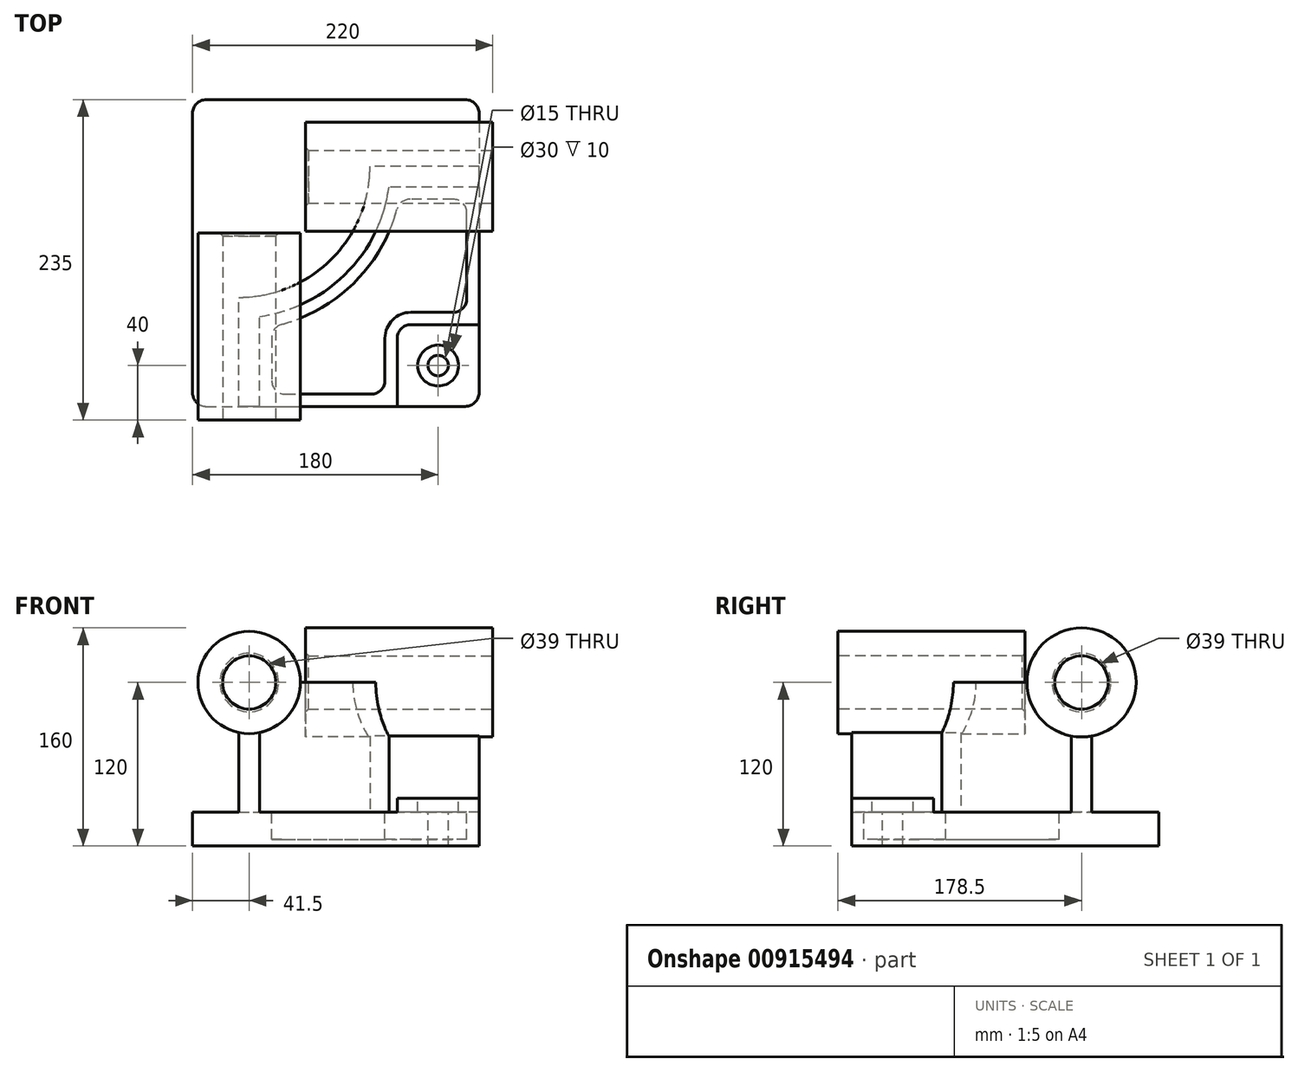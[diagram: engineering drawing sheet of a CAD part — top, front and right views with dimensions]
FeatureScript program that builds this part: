
annotation { "Feature Type Name" : "Feature", "Feature Type Description" : "" }
export const myFeature = defineFeature(function(context is Context, id is Id, definition is map)
    precondition{}
    {
        {
            var Q0;
            Q0=qCreatedBy(makeId("Top.planeOp"),FACE);
            var sketch = newSketch(context, id + "F0", { "sketchPlane" : qUnion([Q0])});
            skLineSegment(sketch, "E0.bottom", {"start": v(-105, 112.5) * mm, "end": v(105, 112.5) * mm});
            skLineSegment(sketch, "E0.top", {"start": v(-105, -112.5) * mm, "end": v(105, -112.5) * mm});
            skLineSegment(sketch, "E0.left", {"start": v(-105, 112.5) * mm, "end": v(-105, -112.5) * mm});
            skLineSegment(sketch, "E0.right", {"start": v(105, 112.5) * mm, "end": v(105, -112.5) * mm});
            skPoint(sketch, "E0.middle", {"position": v(0, 0) * mm});
            skSolve(sketch);
        }
        {
            var Q0;
            Q0=makeQuery(id+"F0.imprint","IMPRINT",FACE,{"disambiguationData":[TD([[makeQuery(id+"F0.imprint","IMPRINT",EDGE,{"derivedFrom":sQuery(id+"F0.wireOp",EDGE,"E0.bottom")}),-1.0]])]});
            extrude(context, id + "F1", {"entities" : qUnion([Q0]), "depth" : 25 * mm, "offsetDistance" : 25 * mm});
        }
        {
            var Q0;
            Q0=makeQuery(id+"F1.opExtrude","CAP_FACE",FACE,{"disambiguationData":[OSD([sQuery(id+"F0.wireOp",EDGE,"E0.bottom"),sQuery(id+"F0.wireOp",EDGE,"E0.top"),sQuery(id+"F0.wireOp",EDGE,"E0.left"),sQuery(id+"F0.wireOp",EDGE,"E0.right")])],"isStart":false});
            var sketch = newSketch(context, id + "F2", { "sketchPlane" : qUnion([Q0])});
            skLineSegment(sketch, "E1", {"start": v(-71, -112.5) * mm, "end": v(-71, -32.5) * mm});
            skLineSegment(sketch, "E2", {"start": v(105, 63.5) * mm, "end": v(25, 63.5) * mm});
            skArc(sketch, "E3", {"start": v(-71, -32.5) * mm, "mid": v(-3.12, -4.38) * mm, "end": v(25, 63.5) * mm});
            skLineSegment(sketch, "E4", {"start": v(-71, 63.5) * mm, "end": v(25, 63.5) * mm, "construction": true});
            skLineSegment(sketch, "E5", {"start": v(-71, 63.5) * mm, "end": v(-71, -32.5) * mm, "construction": true});
            skLineSegment(sketch, "E6.0", {"start": v(-56, -112.5) * mm, "end": v(-56, -46.48) * mm});
            skArc(sketch, "E6.1", {"start": v(-56, -46.48) * mm, "mid": v(7.49, -14.99) * mm, "end": v(38.98, 48.5) * mm});
            skLineSegment(sketch, "E6.2", {"start": v(105, 48.5) * mm, "end": v(38.98, 48.5) * mm});
            skLineSegment(sketch, "E7.0", {"start": v(105, 112.5) * mm, "end": v(105, -112.5) * mm});
            skLineSegment(sketch, "E8.0", {"start": v(-105, -112.5) * mm, "end": v(105, -112.5) * mm});
            skSolve(sketch);
        }
        {
            var Q0;
            {var subQ2=sQuery(id+"F2.wireOp",EDGE,"E1");Q0=makeQuery(id+"F2.imprint","IMPRINT",FACE,{"disambiguationData":[TD([[makeQuery(id+"F2.imprint","IMPRINT",EDGE,{"derivedFrom":subQ2}),-1.0]])]});}
            extrude(context, id + "F3", {"entities" : qUnion([Q0]), "operationType" : NewBodyOperationType.ADD, "depth" : 95 * mm, "offsetDistance" : 25 * mm});
        }
        {
            var Q0;
            Q0=makeQuery(id+"F3.boolean.opBoolean","MERGE",FACE,{"derivedFrom":[makeQuery(id+"F1.opExtrude","SWEPT_FACE",FACE,{"disambiguationData":[OSD([sQuery(id+"F0.wireOp",EDGE,"E0.top")])]}),makeQuery(id+"F3.opExtrude","SWEPT_FACE",FACE,{"disambiguationData":[OSD([sQuery(id+"F2.wireOp",EDGE,"E8.0")])]})]});
            var sketch = newSketch(context, id + "F4", { "sketchPlane" : qUnion([Q0])});
            skCircle(sketch, "E9", {"center": v(-63.5, 120) * mm, "radius": 37.5 * mm});
            skSolve(sketch);
        }
        {
            var Q0;
            Q0 = qSketchRegion(id + "F4", true);
            extrude(context, id + "F5", {"entities" : qUnion([Q0]), "operationType" : NewBodyOperationType.ADD, "depth" : 10 * mm, "offsetDistance" : 25 * mm, "hasSecondDirection" : true, "secondDirectionOppositeDirection" : true, "secondDirectionDepth" : 127.1 * mm});
        }
        {
            var Q0;
            Q0=makeQuery(id+"F3.boolean.opBoolean","MERGE",FACE,{"derivedFrom":[makeQuery(id+"F1.opExtrude","SWEPT_FACE",FACE,{"disambiguationData":[OSD([sQuery(id+"F0.wireOp",EDGE,"E0.right")])]}),makeQuery(id+"F3.opExtrude","SWEPT_FACE",FACE,{"disambiguationData":[OSD([sQuery(id+"F2.wireOp",EDGE,"E7.0")])]})]});
            var sketch = newSketch(context, id + "F6", { "sketchPlane" : qUnion([Q0])});
            skCircle(sketch, "E10", {"center": v(56, 120) * mm, "radius": 40 * mm});
            skSolve(sketch);
        }
        {
            var Q0;
            Q0 = qSketchRegion(id + "F6", true);
            extrude(context, id + "F7", {"entities" : qUnion([Q0]), "operationType" : NewBodyOperationType.ADD, "depth" : 10 * mm, "offsetDistance" : 25 * mm, "hasSecondDirection" : true, "secondDirectionOppositeDirection" : true, "secondDirectionDepth" : 127.1 * mm});
        }
        {
            var Q0;
            {var subQ0=sQuery(id+"F0.wireOp",EDGE,"E0.right");var subQ1=sQuery(id+"F0.wireOp",EDGE,"E0.top");Q0=makeQuery(id+"F3.boolean.opBoolean","SPLIT",FACE,{"disambiguationData":[TD([makeQuery(id+"F3.opExtrude","SWEPT_FACE",FACE,{"disambiguationData":[OSD([sQuery(id+"F2.wireOp",EDGE,"E6.0")])]})])],"derivedFrom":makeQuery(id+"F1.opExtrude","CAP_FACE",FACE,{"disambiguationData":[OSD([sQuery(id+"F0.wireOp",EDGE,"E0.bottom"),subQ1,sQuery(id+"F0.wireOp",EDGE,"E0.left"),subQ0])],"isStart":false})});}
            var sketch = newSketch(context, id + "F8", { "sketchPlane" : qUnion([Q0])});
            skLineSegment(sketch, "E11.bottom", {"start": v(105, -112.5) * mm, "end": v(45, -112.5) * mm});
            skLineSegment(sketch, "E11.top", {"start": v(105, -52.5) * mm, "end": v(45, -52.5) * mm});
            skLineSegment(sketch, "E11.left", {"start": v(105, -112.5) * mm, "end": v(105, -52.5) * mm});
            skLineSegment(sketch, "E11.right", {"start": v(45, -112.5) * mm, "end": v(45, -52.5) * mm});
            skSolve(sketch);
        }
        {
            var Q0;
            Q0 = qSketchRegion(id + "F8", true);
            extrude(context, id + "F9", {"entities" : qUnion([Q0]), "operationType" : NewBodyOperationType.ADD, "depth" : (35 - 25) * mm, "offsetDistance" : 25 * mm});
        }
        {
            var Q0;
            Q0=makeQuery(id+"F9.opExtrude","SWEPT_EDGE",EDGE,{"disambiguationData":[OSD([sQuery(id+"F8.wireOp",EDGE,"E11.top"),sQuery(id+"F8.wireOp",EDGE,"E11.right")])]});
            fillet(context, id + "F10", {"entities" : qUnion([Q0]), "radius" : 10 * mm, "tangentPropagation" : true, "allowEdgeOverflow" : false});
        }
        {
            var Q0;
            {var subQ0=sQuery(id+"F0.wireOp",EDGE,"E0.right");var subQ1=sQuery(id+"F0.wireOp",EDGE,"E0.top");Q0=makeQuery(id+"F3.boolean.opBoolean","SPLIT",FACE,{"disambiguationData":[TD([makeQuery(id+"F3.opExtrude","SWEPT_FACE",FACE,{"disambiguationData":[OSD([sQuery(id+"F2.wireOp",EDGE,"E6.0")])]})])],"derivedFrom":makeQuery(id+"F1.opExtrude","CAP_FACE",FACE,{"disambiguationData":[OSD([sQuery(id+"F0.wireOp",EDGE,"E0.bottom"),subQ1,sQuery(id+"F0.wireOp",EDGE,"E0.left"),subQ0])],"isStart":false})});}
            var sketch = newSketch(context, id + "F11", { "sketchPlane" : qUnion([Q0])});
            skLineSegment(sketch, "E12.0", {"start": v(-47, -54.08) * mm, "end": v(-47, -103.5) * mm});
            skArc(sketch, "E12.1", {"start": v(46.58, 39.5) * mm, "mid": v(13.85, -21.35) * mm, "end": v(-47, -54.08) * mm});
            skLineSegment(sketch, "E12.2", {"start": v(-47, -103.5) * mm, "end": v(36, -103.5) * mm});
            skLineSegment(sketch, "E12.3", {"start": v(96, 39.5) * mm, "end": v(46.58, 39.5) * mm});
            skLineSegment(sketch, "E12.4", {"start": v(36, -103.5) * mm, "end": v(36, -62.5) * mm});
            skArc(sketch, "E12.5", {"start": v(36, -62.5) * mm, "mid": v(41.56, -49.06) * mm, "end": v(55, -43.5) * mm});
            skLineSegment(sketch, "E12.6", {"start": v(55, -43.5) * mm, "end": v(96, -43.5) * mm});
            skLineSegment(sketch, "E12.7", {"start": v(96, -43.5) * mm, "end": v(96, 39.5) * mm});
            skSolve(sketch);
        }
        {
            var Q0;
            Q0=makeQuery(id+"F11.imprint","IMPRINT",FACE,{"disambiguationData":[TD([[makeQuery(id+"F11.imprint","IMPRINT",EDGE,{"derivedFrom":sQuery(id+"F11.wireOp",EDGE,"E12.0")}),1.0]])]});
            extrude(context, id + "F12", {"entities" : qUnion([Q0]), "operationType" : NewBodyOperationType.REMOVE, "oppositeDirection" : true, "depth" : (25 - 5) * mm, "offsetDistance" : 25 * mm});
        }
        {
            var Q0;
            Q0=makeQuery(id+"F9.opExtrude","CAP_FACE",FACE,{"disambiguationData":[OSD([sQuery(id+"F8.wireOp",EDGE,"E11.bottom"),sQuery(id+"F8.wireOp",EDGE,"E11.top"),sQuery(id+"F8.wireOp",EDGE,"E11.left"),sQuery(id+"F8.wireOp",EDGE,"E11.right")])],"isStart":false});
            var sketch = newSketch(context, id + "F13", { "sketchPlane" : qUnion([Q0])});
            skCircle(sketch, "E13", {"center": v(75, -82.5) * mm, "radius": 15 * mm});
            skSolve(sketch);
        }
        {
            var Q0;
            Q0=sQuery(id+"F13.wireOp",VERTEX,"E13.center");
            var Q1;
            Q1=makeQuery(id+"F1.opExtrude","SWEPT_BODY",BODY,{"disambiguationData":[OSD([sQuery(id+"F0.wireOp",EDGE,"E0.bottom"),sQuery(id+"F0.wireOp",EDGE,"E0.top"),sQuery(id+"F0.wireOp",EDGE,"E0.left"),sQuery(id+"F0.wireOp",EDGE,"E0.right")])]});
            hole(context, id + "F14", {"style" : HoleStyle.C_BORE, "endStyle" : HoleEndStyle.THROUGH, "holeDiameter" : 15 * mm, "cBoreDiameter" : 30 * mm, "cBoreDepth" : 10 * mm, "majorDiameter" : 5 * mm, "isTappedThrough" : true, "tappedDepth" : 12 * mm, "tapClearance" : 3, "locations" : qUnion([Q0]), "scope" : qUnion([Q1])});
        }
        {
            var Q0;
            Q0=makeQuery(id+"F12.boolean.opBoolean","COPY",EDGE,{"derivedFrom":makeQuery(id+"F12.opExtrude","SWEPT_EDGE",EDGE,{"disambiguationData":[OSD([sQuery(id+"F11.wireOp",EDGE,"E12.0"),sQuery(id+"F11.wireOp",EDGE,"E12.1")])]})});
            var Q1;
            Q1=makeQuery(id+"F12.boolean.opBoolean","COPY",EDGE,{"derivedFrom":makeQuery(id+"F12.opExtrude","SWEPT_EDGE",EDGE,{"disambiguationData":[OSD([sQuery(id+"F11.wireOp",EDGE,"E12.1"),sQuery(id+"F11.wireOp",EDGE,"E12.3")])]})});
            var Q2;
            Q2=makeQuery(id+"F12.boolean.opBoolean","COPY",EDGE,{"derivedFrom":makeQuery(id+"F12.opExtrude","SWEPT_EDGE",EDGE,{"disambiguationData":[OSD([sQuery(id+"F11.wireOp",EDGE,"E12.0"),sQuery(id+"F11.wireOp",EDGE,"E12.2")])]})});
            var Q3;
            Q3=makeQuery(id+"F12.boolean.opBoolean","COPY",EDGE,{"derivedFrom":makeQuery(id+"F12.opExtrude","SWEPT_EDGE",EDGE,{"disambiguationData":[OSD([sQuery(id+"F11.wireOp",EDGE,"E12.2"),sQuery(id+"F11.wireOp",EDGE,"E12.4")])]})});
            var Q4;
            Q4=makeQuery(id+"F12.boolean.opBoolean","COPY",EDGE,{"derivedFrom":makeQuery(id+"F12.opExtrude","SWEPT_EDGE",EDGE,{"disambiguationData":[OSD([sQuery(id+"F11.wireOp",EDGE,"E12.6"),sQuery(id+"F11.wireOp",EDGE,"E12.7")])]})});
            var Q5;
            Q5=makeQuery(id+"F12.boolean.opBoolean","COPY",EDGE,{"derivedFrom":makeQuery(id+"F12.opExtrude","SWEPT_EDGE",EDGE,{"disambiguationData":[OSD([sQuery(id+"F11.wireOp",EDGE,"E12.3"),sQuery(id+"F11.wireOp",EDGE,"E12.7")])]})});
            fillet(context, id + "F15", {"entities" : qUnion([Q0, Q1, Q2, Q3, Q4, Q5]), "radius" : 10 * mm, "tangentPropagation" : true, "allowEdgeOverflow" : false});
        }
        {
            var Q0;
            Q0=makeQuery(id+"F5.opExtrude","CAP_FACE",FACE,{"disambiguationData":[OSD([sQuery(id+"F4.wireOp",EDGE,"E9")])],"isStart":false});
            var sketch = newSketch(context, id + "F16", { "sketchPlane" : qUnion([Q0])});
            skCircle(sketch, "E14", {"center": v(-63.5, 120) * mm, "radius": 19.5 * mm});
            skSolve(sketch);
        }
        {
            var Q0;
            Q0 = qSketchRegion(id + "F16", true);
            extrude(context, id + "F17", {"entities" : qUnion([Q0]), "operationType" : NewBodyOperationType.REMOVE, "endBound" : BoundingType.THROUGH_ALL, "oppositeDirection" : true, "depth" : 25 * mm, "offsetDistance" : 25 * mm});
        }
        {
            var Q0;
            Q0=makeQuery(id+"F7.opExtrude","CAP_FACE",FACE,{"disambiguationData":[OSD([sQuery(id+"F6.wireOp",EDGE,"E10")])],"isStart":false});
            var sketch = newSketch(context, id + "F18", { "sketchPlane" : qUnion([Q0])});
            skCircle(sketch, "E15", {"center": v(56, 120) * mm, "radius": 19.5 * mm});
            skSolve(sketch);
        }
        {
            var Q0;
            Q0 = qSketchRegion(id + "F18", true);
            extrude(context, id + "F19", {"entities" : qUnion([Q0]), "operationType" : NewBodyOperationType.REMOVE, "endBound" : BoundingType.THROUGH_ALL, "oppositeDirection" : true, "depth" : 25 * mm, "offsetDistance" : 25 * mm});
        }
        {
            var Q0;
            Q0=makeQuery(id+"F19.boolean.opBoolean","COPY",EDGE,{"derivedFrom":makeQuery(id+"F19.opExtrude","CAP_EDGE",EDGE,{"disambiguationData":[OSD([sQuery(id+"F18.wireOp",EDGE,"E15")])],"isStart":true})});
            var Q1;
            Q1=makeQuery(id+"F17.boolean.opBoolean","COPY",EDGE,{"derivedFrom":makeQuery(id+"F17.opExtrude","CAP_EDGE",EDGE,{"disambiguationData":[OSD([sQuery(id+"F16.wireOp",EDGE,"E14")])],"isStart":true})});
            var Q2;
            Q2=makeQuery(id+"F17.boolean.opBoolean","INTERSECT",EDGE,{"derivedFrom":[makeQuery(id+"F5.opExtrude","CAP_FACE",FACE,{"disambiguationData":[OSD([sQuery(id+"F4.wireOp",EDGE,"E9")])],"isStart":true}),makeQuery(id+"F17.opExtrude","SWEPT_FACE",FACE,{"disambiguationData":[OSD([sQuery(id+"F16.wireOp",EDGE,"E14")])]})]});
            var Q3;
            Q3=makeQuery(id+"F19.boolean.opBoolean","INTERSECT",EDGE,{"derivedFrom":[makeQuery(id+"F7.opExtrude","CAP_FACE",FACE,{"disambiguationData":[OSD([sQuery(id+"F6.wireOp",EDGE,"E10")])],"isStart":true}),makeQuery(id+"F19.opExtrude","SWEPT_FACE",FACE,{"disambiguationData":[OSD([sQuery(id+"F18.wireOp",EDGE,"E15")])]})]});
            chamfer(context, id + "F20", {"entities" : qUnion([Q0, Q1, Q2, Q3]), "width" : 2 * mm, "tangentPropagation" : true});
        }
        {
            var Q0;
            Q0=makeQuery(id+"F1.opExtrude","SWEPT_EDGE",EDGE,{"disambiguationData":[OSD([sQuery(id+"F0.wireOp",EDGE,"E0.bottom"),sQuery(id+"F0.wireOp",EDGE,"E0.left")])]});
            var Q1;
            Q1=makeQuery(id+"F1.opExtrude","SWEPT_EDGE",EDGE,{"disambiguationData":[OSD([sQuery(id+"F0.wireOp",EDGE,"E0.bottom"),sQuery(id+"F0.wireOp",EDGE,"E0.right")])]});
            var Q2;
            Q2=makeQuery(id+"F9.boolean.opBoolean","MERGE",EDGE,{"derivedFrom":[makeQuery(id+"F1.opExtrude","SWEPT_EDGE",EDGE,{"disambiguationData":[OSD([sQuery(id+"F0.wireOp",EDGE,"E0.top"),sQuery(id+"F0.wireOp",EDGE,"E0.right")])]}),makeQuery(id+"F9.opExtrude","SWEPT_EDGE",EDGE,{"disambiguationData":[OSD([sQuery(id+"F8.wireOp",EDGE,"E11.bottom"),sQuery(id+"F8.wireOp",EDGE,"E11.left")])]})]});
            var Q3;
            Q3=makeQuery(id+"F1.opExtrude","SWEPT_EDGE",EDGE,{"disambiguationData":[OSD([sQuery(id+"F0.wireOp",EDGE,"E0.top"),sQuery(id+"F0.wireOp",EDGE,"E0.left")])]});
            fillet(context, id + "F21", {"entities" : qUnion([Q0, Q1, Q2, Q3]), "radius" : 10 * mm, "tangentPropagation" : true, "allowEdgeOverflow" : false});
        }
    });
